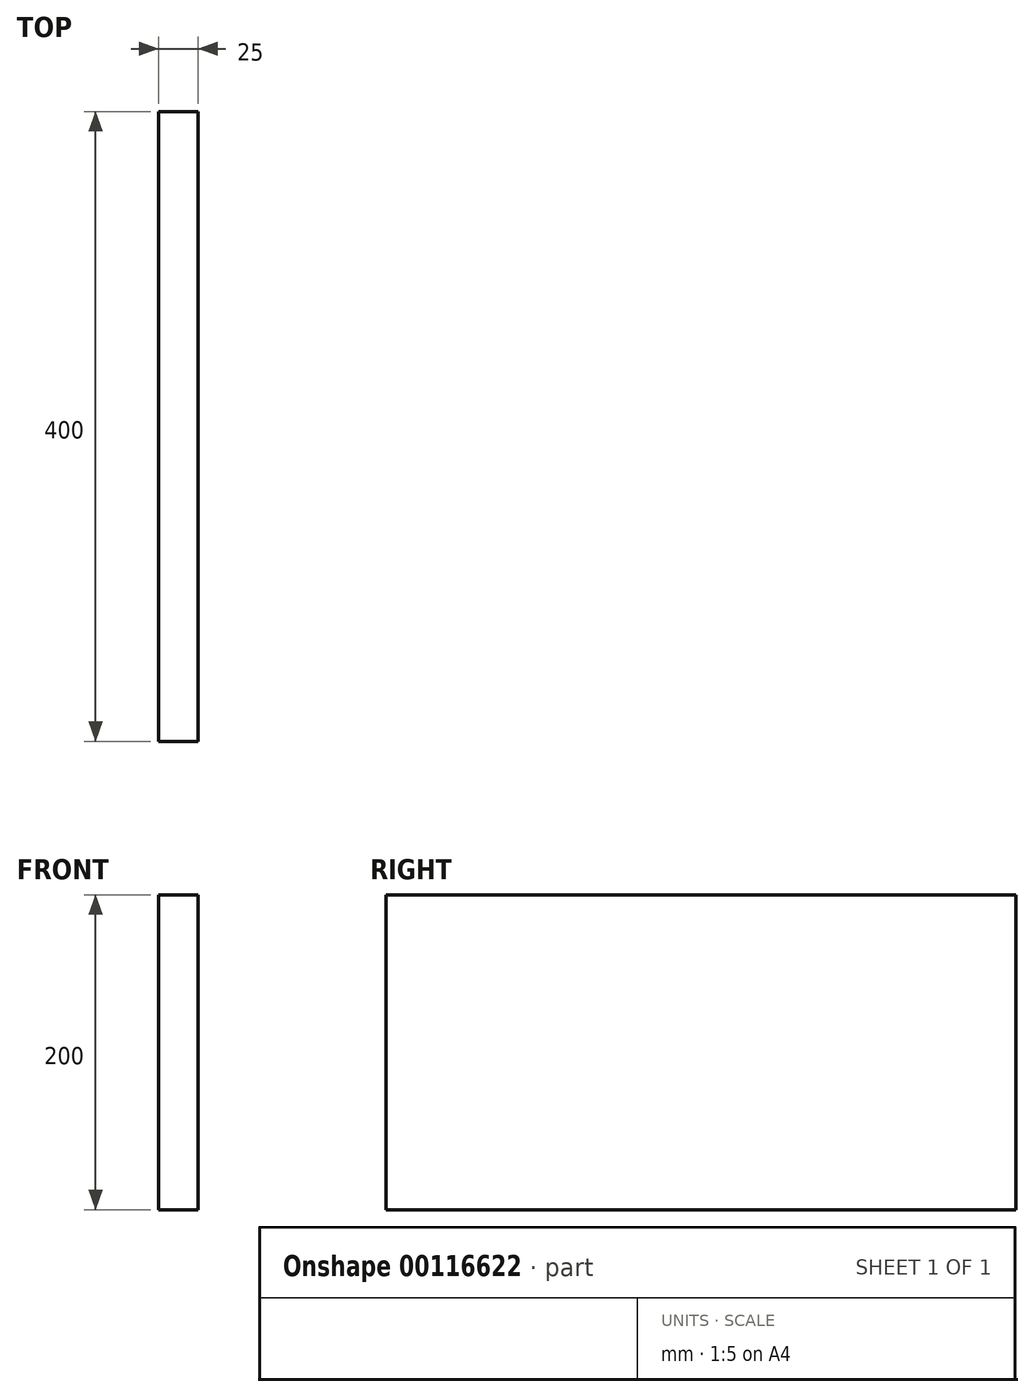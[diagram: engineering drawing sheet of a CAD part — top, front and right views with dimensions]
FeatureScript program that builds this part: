
annotation { "Feature Type Name" : "Feature", "Feature Type Description" : "" }
export const myFeature = defineFeature(function(context is Context, id is Id, definition is map)
    precondition{}
    {
        {
            var Q0;
            Q0=qCreatedBy(makeId("Right.planeOp"),FACE);
            var sketch = newSketch(context, id + "F0", { "sketchPlane" : qUnion([Q0])});
            skLineSegment(sketch, "E0.bottom", {"start": v(-298.64, -35.32) * mm, "end": v(101.36, -35.32) * mm});
            skLineSegment(sketch, "E0.top", {"start": v(-298.64, 164.68) * mm, "end": v(101.36, 164.68) * mm});
            skLineSegment(sketch, "E0.left", {"start": v(-298.64, -35.32) * mm, "end": v(-298.64, 164.68) * mm});
            skLineSegment(sketch, "E0.right", {"start": v(101.36, -35.32) * mm, "end": v(101.36, 164.68) * mm});
            skSolve(sketch);
        }
        {
            var Q0;
            Q0=makeQuery(id+"F0.imprint","IMPRINT",FACE,{"disambiguationData":[TD([[makeQuery(id+"F0.imprint","IMPRINT",EDGE,{"derivedFrom":sQuery(id+"F0.wireOp",EDGE,"E0.bottom")}),1.0]])]});
            extrude(context, id + "F1", {"entities" : qUnion([Q0]), "oppositeDirection" : true, "depth" : 25 * mm});
        }
    });
